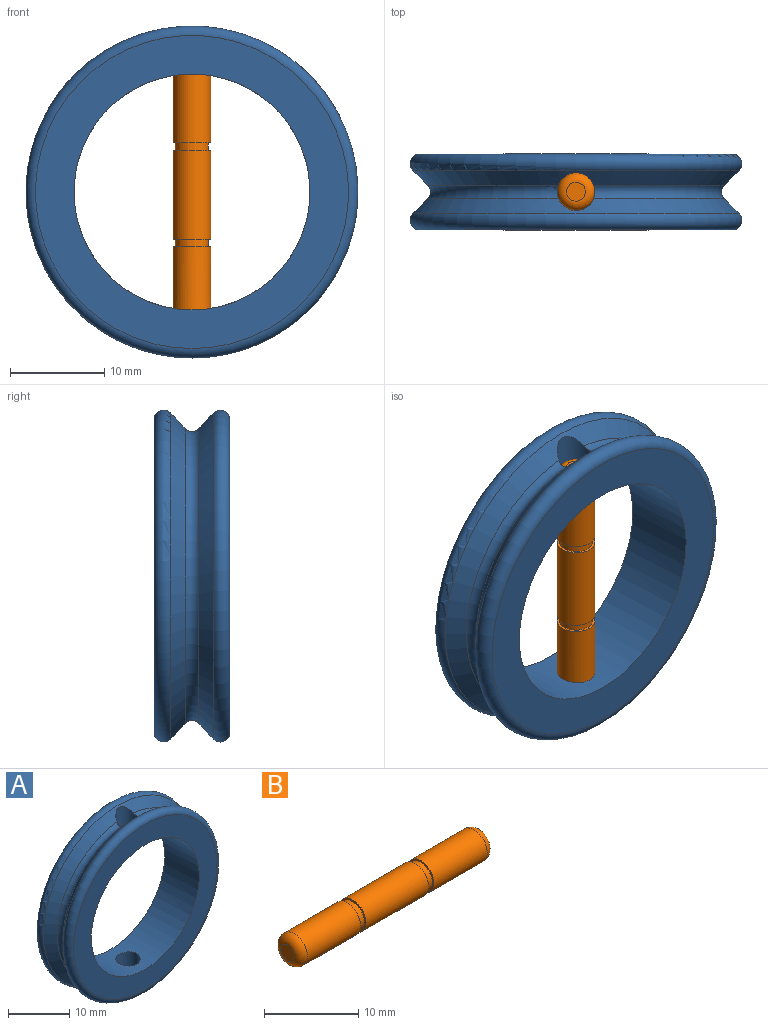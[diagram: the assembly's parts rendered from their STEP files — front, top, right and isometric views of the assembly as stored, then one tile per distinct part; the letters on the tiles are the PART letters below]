
ASSEMBLY  parts=2 mates=1
PART A: 11 faces, bbox 38.1x8x38.1 mm
  f0: cone r=15mm half-angle=45deg, axis (0,-1,0), area 222.6mm2, adj f2,f3,f8,f9,f10
  f1: cone r=15mm half-angle=45deg, axis (0,1,0), area 222.5mm2, adj f2,f3,f7,f9,f10
  f2: torus R=16.41mm, axis (0,-1,0), area 70.4mm2, adj f0,f1,f9,f10
  f3: torus R=16.41mm, axis (0,-1,0), area 70.4mm2, adj f0,f1,f9,f10
  f4: cylinder r=12.5mm len=25mm, axis (0,-1,0), area 603.1mm2, adj f5,f6,f9,f10
  f5: plane 33.17x33.17mm, normal (0,-1,0), area 373.3mm2, adj f4,f8
  f6: plane 33.17x33.17mm, normal (0,1,0), area 373.3mm2, adj f4,f7
  f7: torus R=16.59mm, axis (0,1,0), area 256.3mm2, adj f1,f6
  f8: torus R=16.59mm, axis (0,-1,0), area 256.3mm2, adj f0,f5
  f9: cylinder r=2mm len=4.66mm, axis (0,0,1), area 48.1mm2, adj f0,f1,f2,f3,f4
  f10: cylinder r=2mm len=4.66mm, axis (0,0,-1), area 48.1mm2, adj f0,f1,f2,f3,f4
PART B: 13 faces, bbox 29x4.3x4.3 mm
  f0: cylinder r=2mm len=8mm, axis (1,0,0), area 100.5mm2, adj f6,f11
  f1: cylinder r=2mm len=8mm, axis (1,0,0), area 100.5mm2, adj f7,f12
  f2: plane 4x4mm, normal (1,0,0), area 2.9mm2, adj f3,f8
  f3: cylinder r=2mm len=9.4mm, axis (1,0,0), area 118.1mm2, adj f2,f4
  f4: plane 4x4mm, normal (-1,0,0), area 2.9mm2, adj f3,f5
  f5: cylinder r=1.75mm len=3.5mm, axis (1,0,0), area 8.8mm2, adj f4,f6
  f6: plane 4x4mm, normal (1,0,0), area 2.9mm2, adj f0,f5
  f7: plane 4x4mm, normal (-1,0,0), area 2.9mm2, adj f1,f8
  f8: cylinder r=1.75mm len=3.5mm, axis (1,0,0), area 8.8mm2, adj f2,f7
  f9: plane 2x2mm, normal (1,0,0), area 3.1mm2, adj f12
  f10: plane 2x2mm, normal (-1,0,0), area 3.1mm2, adj f11
  f11: torus R=1mm, axis (-1,0,0), area 16.2mm2, adj f0,f10
  f12: torus R=1mm, axis (1,0,0), area 16.2mm2, adj f1,f9
PLACE A t=(-0.27,-3.47,8.95)mm
PLACE B rot(axis=(0.71,0,0.71),180deg) t=(-0.27,-3.47,-8.84)mm
MATE slider B.f0 <-> A.f9  axis (0,0,1) through (-0.27,-3.47,3.96)mm
